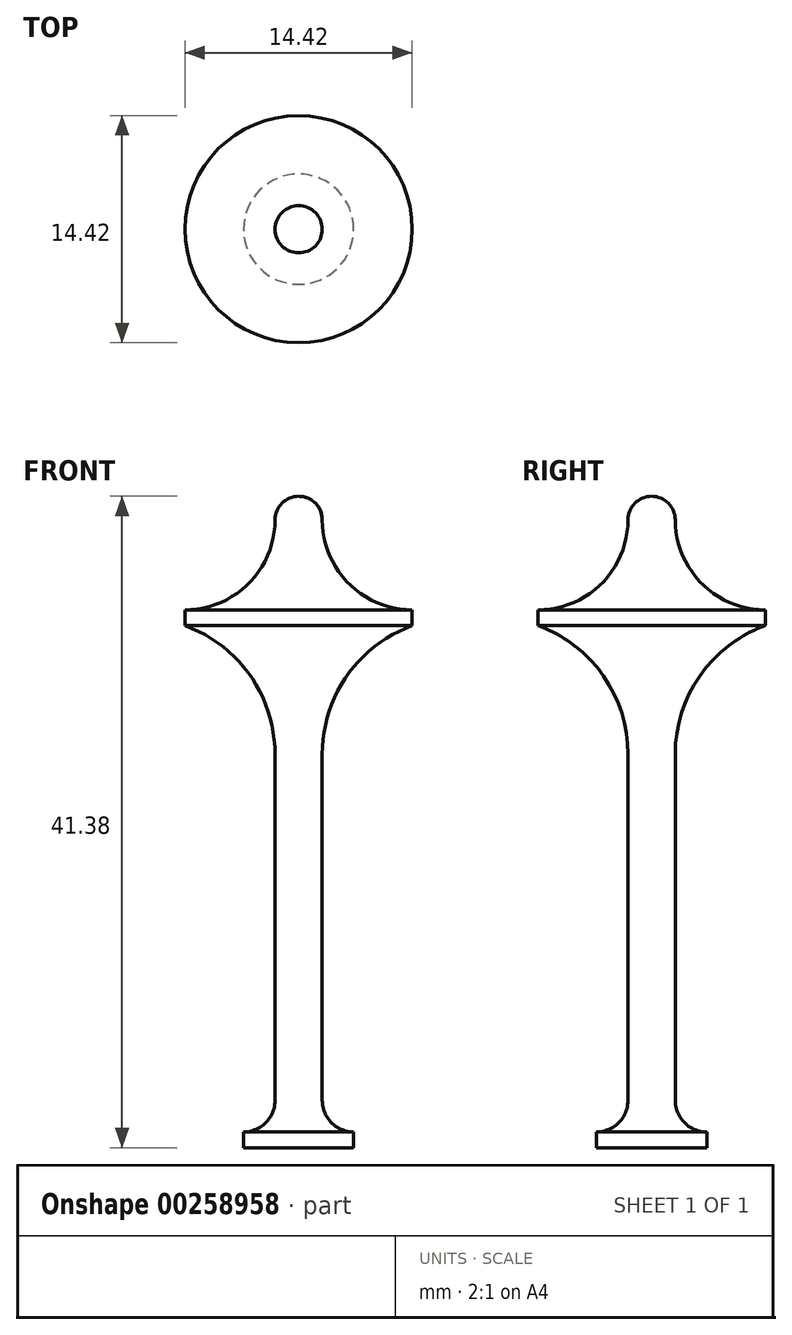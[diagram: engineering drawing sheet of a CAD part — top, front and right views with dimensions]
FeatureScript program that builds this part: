
annotation { "Feature Type Name" : "Feature", "Feature Type Description" : "" }
export const myFeature = defineFeature(function(context is Context, id is Id, definition is map)
    precondition{}
    {
        {
            var Q0;
            Q0=qCreatedBy(makeId("Front.planeOp"),FACE);
            var sketch = newSketch(context, id + "F0", { "sketchPlane" : qUnion([Q0])});
            skLineSegment(sketch, "E0", {"start": v(0, 0) * mm, "end": v(3.5, 0) * mm});
            skLineSegment(sketch, "E1", {"start": v(3.5, 0) * mm, "end": v(3.5, 1) * mm});
            skLineSegment(sketch, "E2", {"start": v(3.5, 1) * mm, "end": v(3.5, 1) * mm});
            skLineSegment(sketch, "E3", {"start": v(1.5, 3) * mm, "end": v(1.5, 25) * mm});
            skArc(sketch, "E4", {"start": v(7.21, 33.16) * mm, "mid": v(3.07, 29.98) * mm, "end": v(1.5, 25) * mm});
            skLineSegment(sketch, "E5", {"start": v(7.21, 33.16) * mm, "end": v(7.21, 34.16) * mm});
            skArc(sketch, "E6", {"start": v(1.5, 39.88) * mm, "mid": v(3.17, 35.83) * mm, "end": v(7.21, 34.16) * mm});
            skArc(sketch, "E7", {"start": v(1.5, 39.88) * mm, "mid": v(1.06, 40.94) * mm, "end": v(0, 41.38) * mm});
            skLineSegment(sketch, "E8", {"start": v(0, 0) * mm, "end": v(0, 67.84) * mm});
            skPoint(sketch, "E9.orphan", {"position": v(0, 38.38) * mm});
            skPoint(sketch, "E10.visualSharp", {"position": v(1.5, 1) * mm});
            skArc(sketch, "E10.filletArc", {"start": v(1.5, 3) * mm, "mid": v(2.09, 1.59) * mm, "end": v(3.5, 1) * mm});
            skLineSegment(sketch, "E11", {"start": v(7.21, 33.16) * mm, "end": v(27.46, 40.53) * mm, "construction": true});
            skLineSegment(sketch, "E12", {"start": v(7.21, 33.16) * mm, "end": v(36.3, 33.16) * mm, "construction": true});
            skSolve(sketch);
        }
        {
            var Q0;
            Q0 = qSketchRegion(id + "F0", true);
            var Q1;
            Q1=sQuery(id+"F0.wireOp",EDGE,"E8");
            revolve(context, id + "F1", {"entities" : qUnion([Q0]), "axis" : qUnion([Q1]), "revolveType" : RevolveType.FULL});
        }
    });
